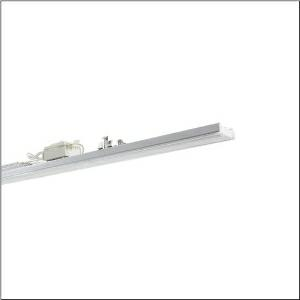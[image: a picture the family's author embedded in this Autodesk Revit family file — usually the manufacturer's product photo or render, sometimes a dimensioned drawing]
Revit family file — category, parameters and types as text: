
# Revit family: licross_r__11_recessed_ho_51te12cn4c5m_5e61
name_source: partatom
category: Lighting Fixtures
units: mm (PartAtom-declared; Revit-internal decimal feet)

## family parameters
Cut with Voids When Loaded = No
Host = Face
Light Source = No
Part Type = Normal
Room Calculation Point = No
Round Connector Dimension = Use Diameter
Shared = No

## types (1)
- --- (1 x LED, 12740 lm, 66.5 W, 4000K)
    Apparent Load = 67 VA
    CIE Flux Codes = 66 91 98 100 100
    Color Rendering = 80
    Color Temperature = 4000K
    Default Elevation = 1800 mm
    Description = Licross® 11 Recessed HO, luminaire insert, of sheet steel, galvanised, coil coated, white, length: 1.500mm, width: 66mm, height: 67mm, LED rated luminous flux: 12.740lm, light colour: 840, control gear: ON/OFF Multilumen, CLOi, with plug, 3-pole, with phase selection, mains connection: 220..240V, AC, 50/60Hz, start of lifetime: 67W, end of service life: 75W, halogen-free wiring, primary optical cover: cover, of PMMA, light emission: direct distribution, primary light characteristic: symmetric, protection rating (complete): IP54, insulation class (complete): insulation class I (protective earthing), certification: CE, ENEC, VDE, UKCA, protection symbol: D if used in an environment with non-conductive dust loads with corresponding accessories, impact resistance: IK06, permissible ambient temperature for indoor applications: -35..+35°C, corresponds to IFS (International Featured Standards) requirements for safety and quality in the food industry, reducing of maximum allowable ambient temperature of 5°C with ceiling mounting, LABS conformity tested according to VDMA 24364:2018-05, packaging unit: 1 piece
    Height = 58 mm
    Lamp = 1 x LED
    Lamp Light Flux = 12740 lm
    Lamp Power = 66.5 W
    Lamp count = 1
    Length = 1500 mm
    Luminous efficacy = 192 lm/W
    Manufacturer = Siteco
    ModVariant = No
    Model = 51TE12CN4C5M
    Mounting Place = Ceiling
    Mounting Type = Pendant
    Number of Poles = 1
    OnlyDefault = Yes
    Power Factor = 1
    Product Name = Licross® 11 Recessed HO
    Product group = luminaire insert
    ProductGroupID = 902
    Protection Class = Protection class I
    Protection Degree = IP 54
    RLX_Detail_Level = 1
    RLX_Emergency_Light_Flux = 0 lm
    RLX_Emergency_Type = 0
    RLX_Emergency_Type_DB = No
    RlxData = <blob elided: 22241 chars, md5=1a9e57fe>
    Socket = socket
    Standby Power = 0 W
    System Light Flux = 12740 lm
    System Power = 67 W
    Type Comments = factory setting: luminous flux: 100 % | (A | C | E) | 156 mA
    Type Image = l_1296930.jpg
    URL = http://relux.com
    VarID = @adj_085026
    Voltage = 0 V
    Weight = 0.00 kg
    Width = 66 mm

## geometry (parser evidence)
native form markers: Blend x4, Sweep x11
no freeform markers — native parametric forms only
